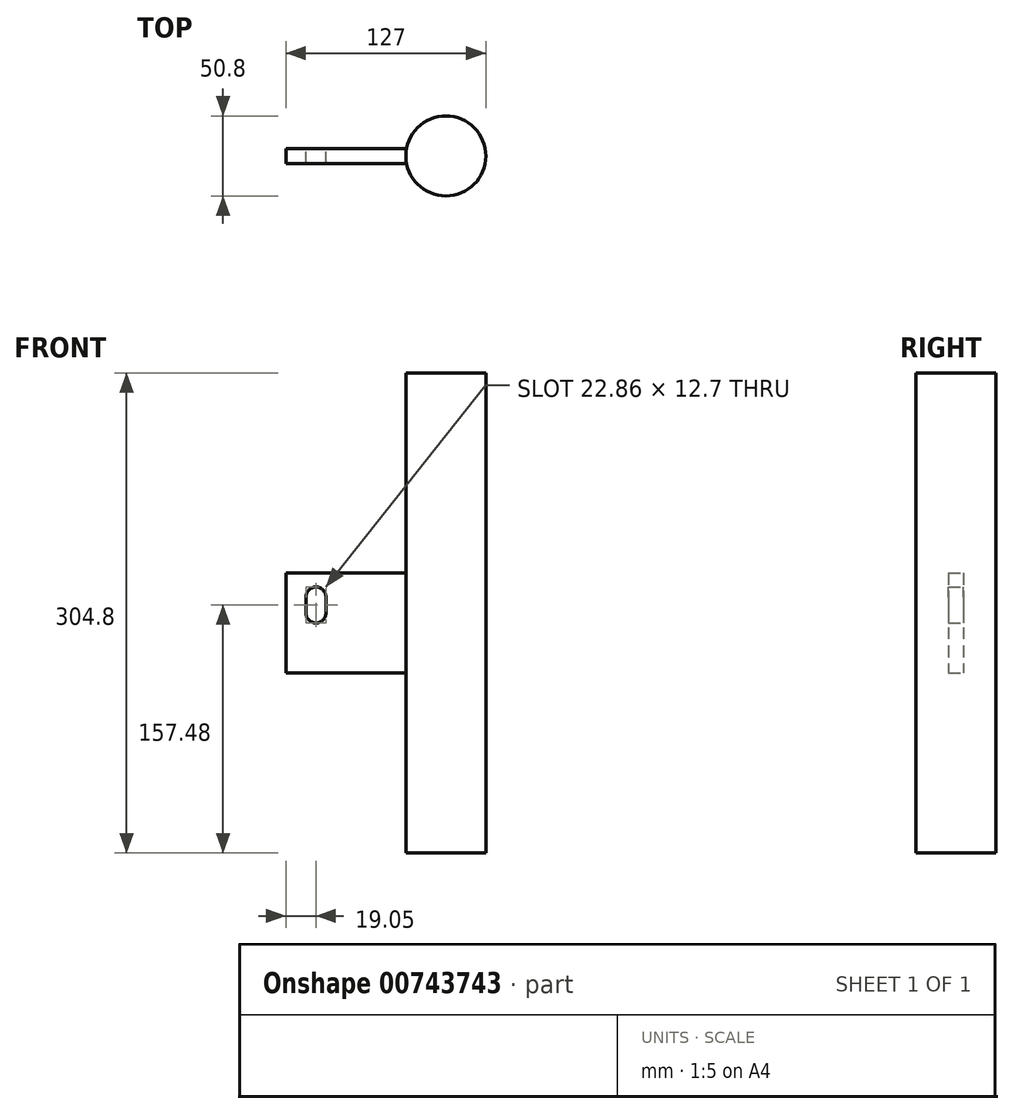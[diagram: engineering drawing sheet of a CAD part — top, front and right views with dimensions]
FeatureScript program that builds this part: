
annotation { "Feature Type Name" : "Feature", "Feature Type Description" : "" }
export const myFeature = defineFeature(function(context is Context, id is Id, definition is map)
    precondition{}
    {
        {
            var Q0;
            Q0=qCreatedBy(makeId("Top.planeOp"),FACE);
            var sketch = newSketch(context, id + "F0", { "sketchPlane" : qUnion([Q0])});
            skCircle(sketch, "E0", {"center": v(0, 0) * mm, "radius": 25.4 * mm});
            skSolve(sketch);
        }
        {
            var Q0;
            Q0 = qSketchRegion(id + "F0", true);
            extrude(context, id + "F1", {"entities" : qUnion([Q0]), "depth" : 304.8 * mm, "offsetDistance" : 25.4 * mm, "symmetric" : true});
        }
        {
            var Q0;
            Q0=qCreatedBy(makeId("Front.planeOp"),FACE);
            var sketch = newSketch(context, id + "F2", { "sketchPlane" : qUnion([Q0])});
            skLineSegment(sketch, "E1.bottom", {"start": v(-101.6, 25.4) * mm, "end": v(-25.4, 25.4) * mm});
            skLineSegment(sketch, "E1.top", {"start": v(-101.6, -38.1) * mm, "end": v(-25.4, -38.1) * mm});
            skLineSegment(sketch, "E1.left", {"start": v(-101.6, 25.4) * mm, "end": v(-101.6, -38.1) * mm});
            skLineSegment(sketch, "E1.right", {"start": v(-25.4, 25.4) * mm, "end": v(-25.4, -38.1) * mm});
            skArc(sketch, "E2", {"start": v(-88.9, 0) * mm, "mid": v(-82.55, -6.35) * mm, "end": v(-76.2, 0) * mm});
            skArc(sketch, "E3", {"start": v(-76.2, 10.16) * mm, "mid": v(-82.55, 16.51) * mm, "end": v(-88.9, 10.16) * mm});
            skLineSegment(sketch, "E4", {"start": v(-88.9, 10.16) * mm, "end": v(-88.9, 0) * mm});
            skLineSegment(sketch, "E5", {"start": v(-76.2, 10.16) * mm, "end": v(-76.2, 0) * mm});
            skSolve(sketch);
        }
        {
            var Q0;
            Q0 = qSketchRegion(id + "F2", true);
            extrude(context, id + "F3", {"entities" : qUnion([Q0]), "depth" : 9.52 * mm, "offsetDistance" : 25.4 * mm, "symmetric" : true});
        }
    });
